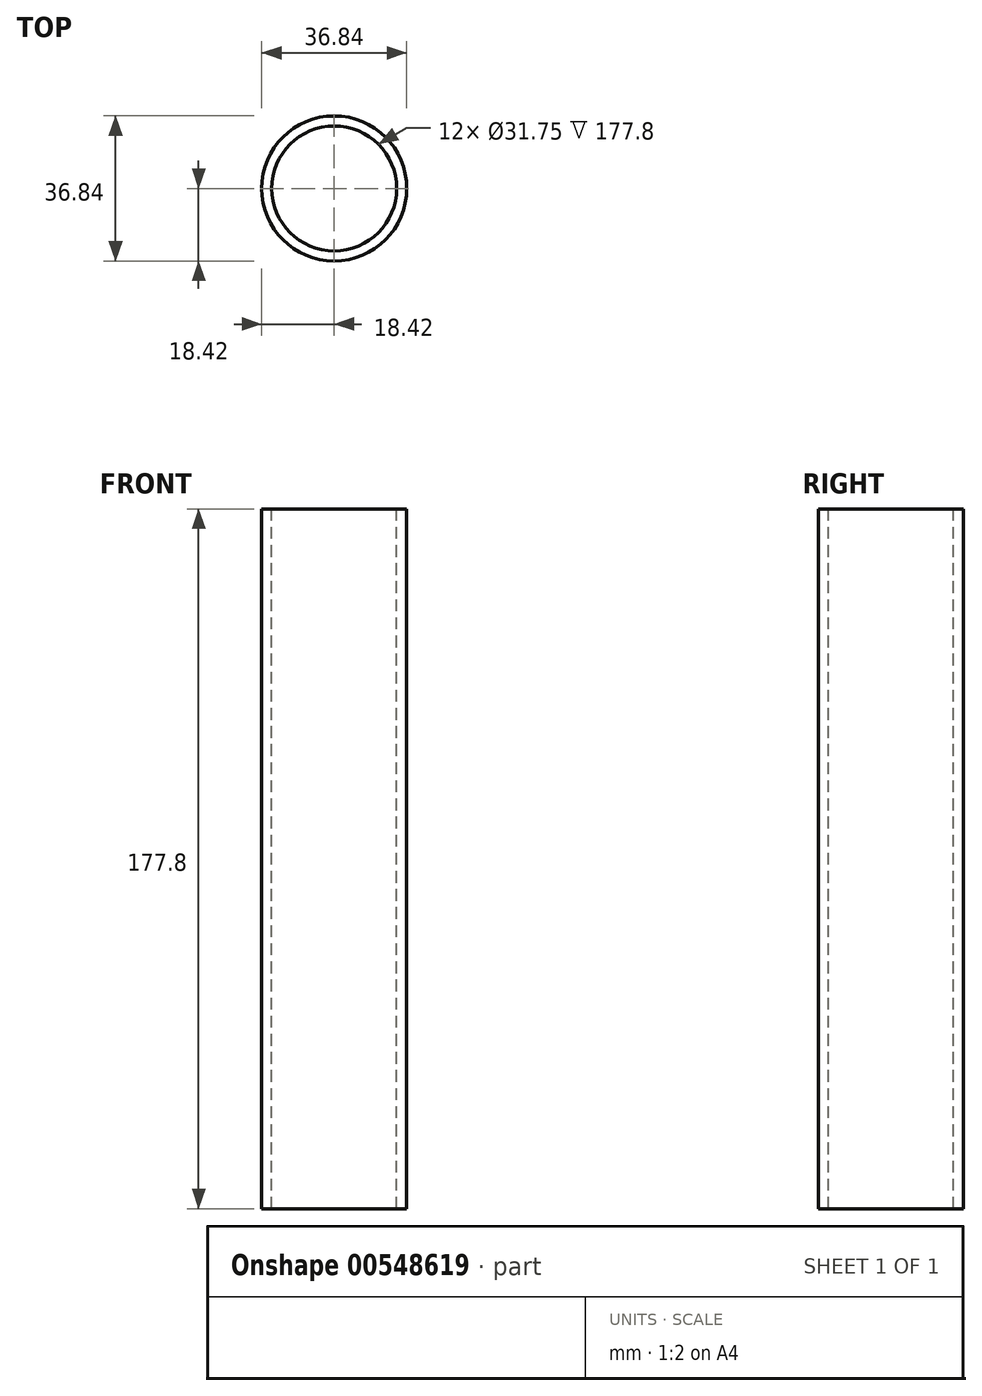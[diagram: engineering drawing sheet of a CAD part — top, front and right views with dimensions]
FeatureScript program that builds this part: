
annotation { "Feature Type Name" : "Feature", "Feature Type Description" : "" }
export const myFeature = defineFeature(function(context is Context, id is Id, definition is map)
    precondition{}
    {
        {
            var Q0;
            Q0=qCreatedBy(makeId("Front.planeOp"),FACE);
            var sketch = newSketch(context, id + "F0", { "sketchPlane" : qUnion([Q0])});
            skLineSegment(sketch, "E0", {"start": v(15.88, 84.72) * mm, "end": v(18.41, 84.72) * mm});
            skLineSegment(sketch, "E1", {"start": v(18.41, 84.72) * mm, "end": v(18.42, -93.08) * mm});
            skLineSegment(sketch, "E2", {"start": v(18.42, -93.08) * mm, "end": v(15.88, -93.08) * mm});
            skLineSegment(sketch, "E3", {"start": v(15.88, -93.08) * mm, "end": v(15.88, 84.72) * mm});
            skSolve(sketch);
        }
        {
            var Q0;
            Q0=qCreatedBy(makeId("Front.planeOp"),FACE);
            var sketch = newSketch(context, id + "F1", { "sketchPlane" : qUnion([Q0])});
            skLineSegment(sketch, "E4", {"start": v(0, 76.47) * mm, "end": v(0, -85.7) * mm});
            skSolve(sketch);
        }
        {
            var Q0;
            Q0=makeQuery(id+"F0.imprint","IMPRINT",FACE,{"disambiguationData":[TD([[makeQuery(id+"F0.imprint","IMPRINT",EDGE,{"derivedFrom":sQuery(id+"F0.wireOp",EDGE,"E0")}),-1.0]])]});
            var Q1;
            Q1=sQuery(id+"F1.wireOp",EDGE,"E4");
            revolve(context, id + "F2", {"entities" : qUnion([Q0]), "axis" : qUnion([Q1]), "revolveType" : RevolveType.FULL});
        }
    });
